# Revit family: Sanitary_Bath-Spas_AXOR_42006XXX-AXOR-Universal-Basins-Bathtubs__88
name_source: partatom
category: Plumbing Fixtures
revit_build: Autodesk Revit 2018 (Build: 20170223_1515(x64)
units: mm (PartAtom-declared; Revit-internal decimal feet)

## family parameters
Always vertical = Yes
Cut with Voids When Loaded = No
OmniClass Number = 23.31.15.11
OmniClass Title = Bath Shower Units
Part Type = Normal
Room Calculation Point = No
Round Connector Dimension = Use Diameter
Shared = No
Work Plane-Based = No

## types (5) — shared parameters
BIMobject category = Bath & Spas
Description = AXOR Universal Basins & Bathtubs Bathtub 1900/850 with shelf
Design country = Germany
Edition number = 1
IFC Classification = Sanitary Terminal
Manufacturer = AXOR
Manufacturer country = Germany
Manufacturer name = AXOR
Model = 42006XXX
OmniClass Code = 23-31 15 11
OmniClass Description = Bath Shower Units
Product Guid = 48c45e55-3619-45f6-934b-c79688c95794
Product SKU = 42006XXX
Product data url = https://bimobject.com
Product family = AXOR Universal Basins & Bathtub
Product group = Bathtub
Product name = 42006XXX AXOR Universal Basins & Bathtubs Bathtub 1900/850 with shelf
Product url = https://www.axor-design.com
QR code = https://bimobject.com
URL = https://www.axor-design.com
Version = 1

## per-type parameters (varying)
| type | Material |
| 000 Chrome | AXOR - Metal - 000 Chrome |
| 140 Brushed Bronze | AXOR - Metal - 140 Brushed Bronze |
| 340 Brushed Black Chrome | AXOR - Metal - 340 Brushed Black Chrome |
| 670 Matte Black | AXOR - Metal - 670 Matte Black |
| 990 Polished Gold Optic | AXOR - Metal - 990 Polished Gold Optic |

## geometry (parser evidence)
native form markers: Sweep x2
no freeform markers — native parametric forms only
